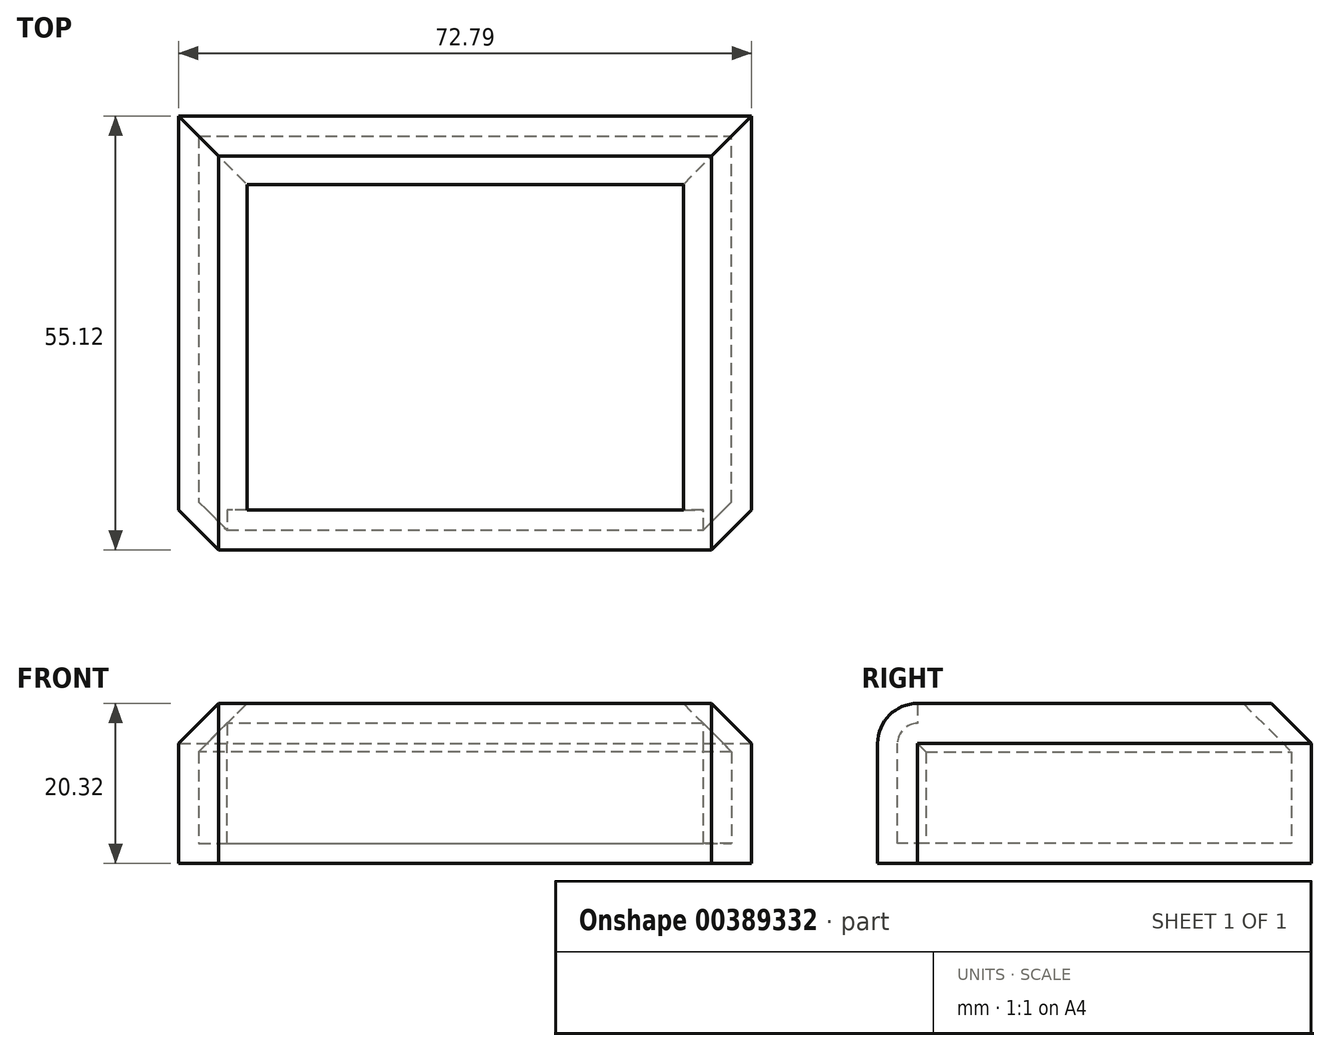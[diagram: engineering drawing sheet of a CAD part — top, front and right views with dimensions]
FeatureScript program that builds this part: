
annotation { "Feature Type Name" : "Feature", "Feature Type Description" : "" }
export const myFeature = defineFeature(function(context is Context, id is Id, definition is map)
    precondition{}
    {
        {
            var Q0;
            Q0=qCreatedBy(makeId("Top.planeOp"),FACE);
            var sketch = newSketch(context, id + "F0", { "sketchPlane" : qUnion([Q0])});
            skLineSegment(sketch, "E0.bottom", {"start": v(-114.96, 35.38) * mm, "end": v(-42.17, 35.38) * mm});
            skLineSegment(sketch, "E0.top", {"start": v(-114.96, -19.74) * mm, "end": v(-42.17, -19.74) * mm});
            skLineSegment(sketch, "E0.left", {"start": v(-114.96, 35.38) * mm, "end": v(-114.96, -19.74) * mm});
            skLineSegment(sketch, "E0.right", {"start": v(-42.17, 35.38) * mm, "end": v(-42.17, -19.74) * mm});
            skSolve(sketch);
        }
        {
            var Q0;
            Q0 = qSketchRegion(id + "F0", true);
            extrude(context, id + "F1", {"entities" : qUnion([Q0]), "depth" : 20.32 * mm});
        }
        {
            var Q0;
            Q0=makeQuery(id+"F1.opExtrude","CAP_EDGE",EDGE,{"disambiguationData":[OSD([sQuery(id+"F0.wireOp",EDGE,"E0.top")])],"isStart":false});
            fillet(context, id + "F2", {"entities" : qUnion([Q0]), "radius" : 5.08 * mm, "tangentPropagation" : true, "allowEdgeOverflow" : false});
        }
        {
            var Q0;
            Q0=makeQuery(id+"F1.opExtrude","CAP_FACE",FACE,{"disambiguationData":[OSD([sQuery(id+"F0.wireOp",EDGE,"E0.bottom"),sQuery(id+"F0.wireOp",EDGE,"E0.top"),sQuery(id+"F0.wireOp",EDGE,"E0.left"),sQuery(id+"F0.wireOp",EDGE,"E0.right")])],"isStart":false});
            chamfer(context, id + "F3", {"entities" : qUnion([Q0]), "width" : 5.08 * mm, "tangentPropagation" : true});
        }
        {
            var Q0;
            Q0=makeQuery(id+"F1.opExtrude","CAP_FACE",FACE,{"disambiguationData":[OSD([sQuery(id+"F0.wireOp",EDGE,"E0.bottom"),sQuery(id+"F0.wireOp",EDGE,"E0.top"),sQuery(id+"F0.wireOp",EDGE,"E0.left"),sQuery(id+"F0.wireOp",EDGE,"E0.right")])],"isStart":false});
            shell(context, id + "F4", {"entities" : qUnion([Q0]), "thickness" : 2.54 * mm});
        }
    });
